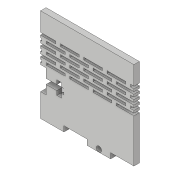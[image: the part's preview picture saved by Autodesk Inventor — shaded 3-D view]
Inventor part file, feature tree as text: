
AUTODESK INVENTOR PART (.ipt)
format: ipt  version: 2017 (Build 210142000, 142)  size: 301,056 bytes
history: native  units: in
note: dims shown in document units (in); Inventor stores cm internally (conversion verified against a paired STEP export)
features: extrude x5, sketch x5
ambient origin geometry x8: Origin, YZ Plane, XZ Plane, XY Plane, X Axis, Y Axis, Z Axis, Center Point
bodies: Solid1 (feature_tree)
feature tree (10):
  extrude  "Extrusion1"  Depth=2.0in
  extrude  "Extrusion2"  Depth=0.5in
  extrude  "Extrusion4"  Depth=0.5in
  extrude  "Extrusion6"  Depth=0.117in
  extrude  "Extrusion7"  Depth=0.5in
  sketch  "Sketch1"  dims[d0=2.0in d1=2.0in]
  sketch  "Sketch2"  dims[d2=0.117in d3=0.0in d4=0.5in]
  sketch  "Sketch3"  dims[d5=0.117in d6=0.5in]
  sketch  "Sketch4"  dims[d7=0.117in d8=0.117in]
  sketch  "Sketch5"  dims[d9=0.5in d10=0.5in d11=0.117in d12=0.0in d14=0.05in d15=0.4in d16=0.05in d17=0.4in d18=0.05in d19=0.05in d20=0.4in d21=0.05in d22=0.2in d23=0.1in d24=0.05in d25=0.05in d26=0.4in d27=0.0in d28=0.1in d29=1.1811in d31=1.0in d32=1.1811in d34=0.2in d37=1.025in d40=0.117in d41=0.0in d43=0.113in d44=0.25in d45=0.0585in d50=0.117in d51=0.0in d52=0.23in d53=0.053in d54=0.1in d55=0.1in d56=0.113in d57=0.113in d58=0.088in d59=0.088in d60=0.088in d61=0.1915in d62=0.117in d63=0.0in]
